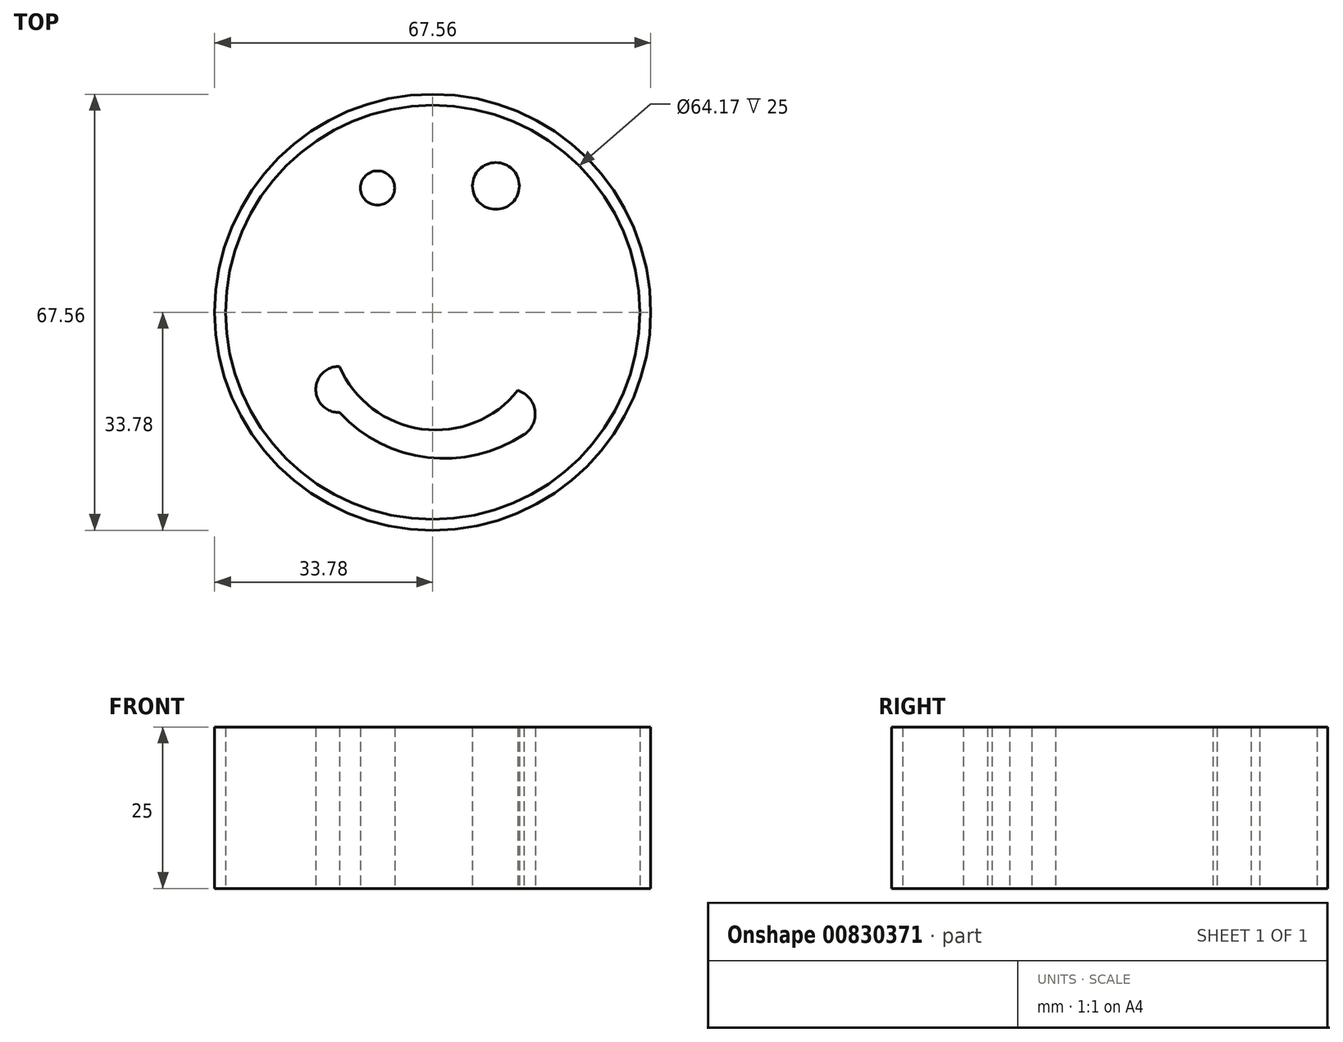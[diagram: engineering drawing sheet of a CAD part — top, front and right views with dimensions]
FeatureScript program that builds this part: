
annotation { "Feature Type Name" : "Feature", "Feature Type Description" : "" }
export const myFeature = defineFeature(function(context is Context, id is Id, definition is map)
    precondition{}
    {
        {
            var Q0;
            Q0=qCreatedBy(makeId("Top.planeOp"),FACE);
            var sketch = newSketch(context, id + "F0", { "sketchPlane" : qUnion([Q0])});
            skCircle(sketch, "E0", {"center": v(0, 0) * mm, "radius": 32.08 * mm});
            skArc(sketch, "E1", {"start": v(-14.45, -8.39) * mm, "mid": v(-1.68, -18.1) * mm, "end": v(13.2, -12.12) * mm});
            skArc(sketch, "E2", {"start": v(-14.45, -15.53) * mm, "mid": v(-0.79, -22.5) * mm, "end": v(14.13, -18.95) * mm});
            skArc(sketch, "E3", {"start": v(14.13, -18.95) * mm, "mid": v(15.85, -15.24) * mm, "end": v(13.2, -12.12) * mm});
            skArc(sketch, "E4", {"start": v(-14.45, -8.39) * mm, "mid": v(-18.11, -11.96) * mm, "end": v(-14.45, -15.53) * mm});
            skCircle(sketch, "E5.0", {"center": v(0, 0) * mm, "radius": 36.78 * mm});
            skCircle(sketch, "E6", {"center": v(-8.54, 19.26) * mm, "radius": 2.65 * mm});
            skCircle(sketch, "E7", {"center": v(9.79, 19.57) * mm, "radius": 3.62 * mm});
            skArc(sketch, "E8.0", {"start": v(-12.2, -5.82) * mm, "mid": v(-20.85, -10.13) * mm, "end": v(-15.84, -18.4) * mm});
            skArc(sketch, "E8.1", {"start": v(-12.2, -5.82) * mm, "mid": v(-1.23, -15.13) * mm, "end": v(11.77, -8.95) * mm});
            skArc(sketch, "E8.2", {"start": v(15.78, -21.46) * mm, "mid": v(18.56, -13.67) * mm, "end": v(11.77, -8.95) * mm});
            skArc(sketch, "E8.3", {"start": v(-15.84, -18.4) * mm, "mid": v(-0.57, -25.55) * mm, "end": v(15.78, -21.46) * mm});
            skCircle(sketch, "E9.0", {"center": v(0, 0) * mm, "radius": 29.08 * mm});
            skCircle(sketch, "E10.0", {"center": v(0, 0) * mm, "radius": 33.78 * mm});
            skSolve(sketch);
        }
        {
            var Q0;
            Q0=makeQuery(id+"F0.imprint","IMPRINT",FACE,{"disambiguationData":[TD([[makeQuery(id+"F0.imprint","IMPRINT",EDGE,{"derivedFrom":sQuery(id+"F0.wireOp",EDGE,"E0")}),-1.0]])]});
            var Q1;
            Q1=makeQuery(id+"F0.imprint","IMPRINT",FACE,{"disambiguationData":[TD([[makeQuery(id+"F0.imprint","IMPRINT",EDGE,{"derivedFrom":sQuery(id+"F0.wireOp",EDGE,"E6")}),1.0]])]});
            var Q2;
            Q2=makeQuery(id+"F0.imprint","IMPRINT",FACE,{"disambiguationData":[TD([[makeQuery(id+"F0.imprint","IMPRINT",EDGE,{"derivedFrom":sQuery(id+"F0.wireOp",EDGE,"E7")}),1.0]])]});
            var Q3;
            Q3=makeQuery(id+"F0.imprint","IMPRINT",FACE,{"disambiguationData":[TD([[makeQuery(id+"F0.imprint","IMPRINT",EDGE,{"derivedFrom":sQuery(id+"F0.wireOp",EDGE,"E1")}),-1.0]])]});
            extrude(context, id + "F1", {"entities" : qUnion([Q0, Q1, Q2, Q3]), "depth" : 25 * mm, "offsetDistance" : 25 * mm});
        }
    });
